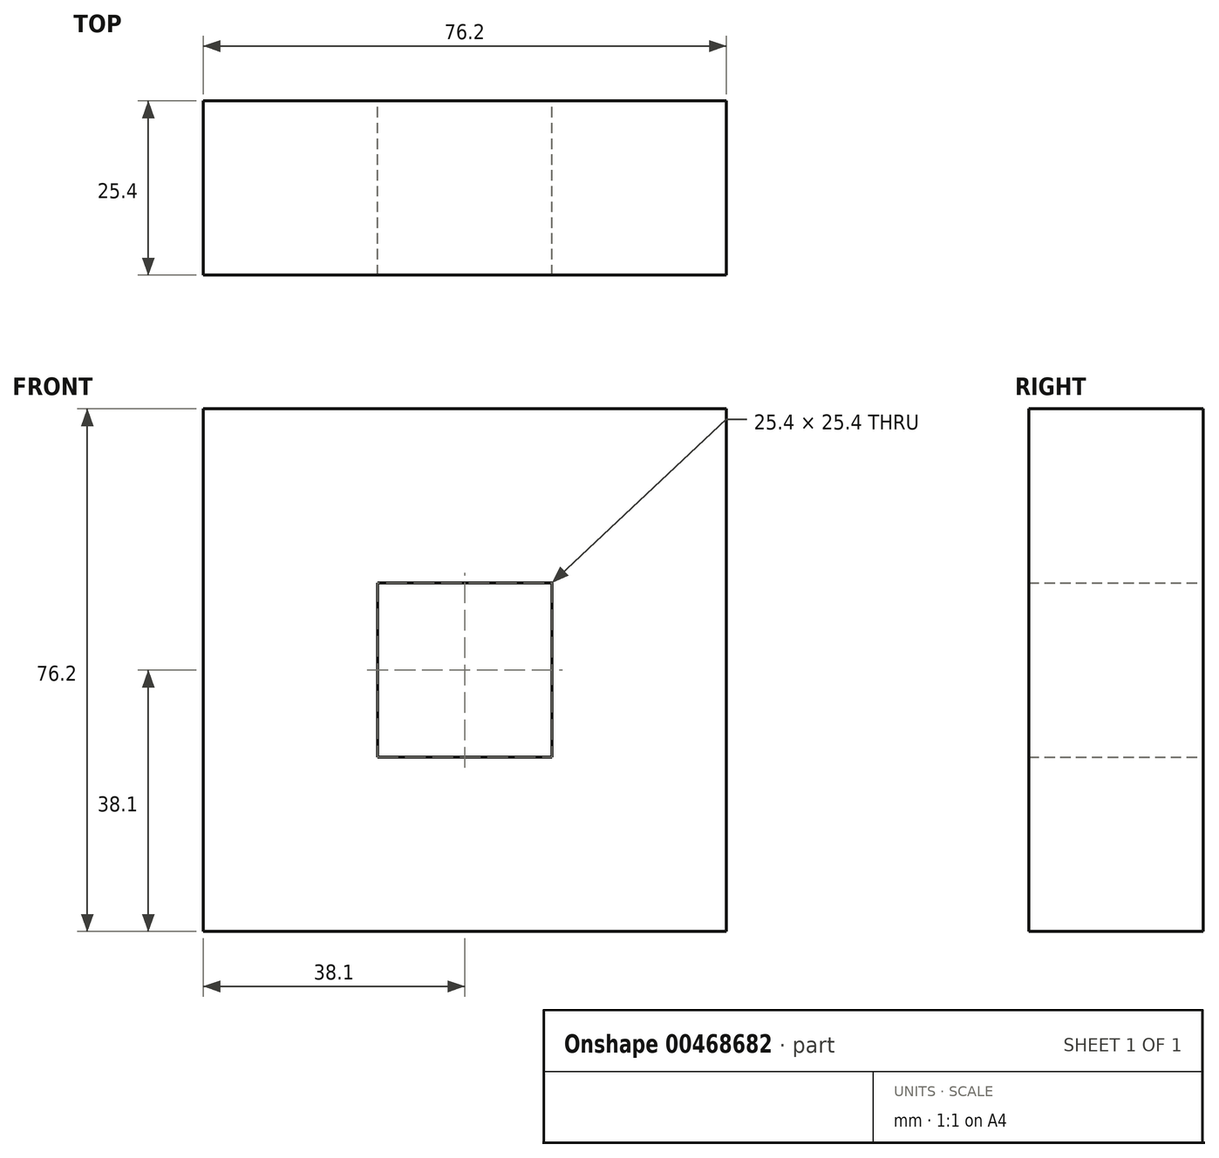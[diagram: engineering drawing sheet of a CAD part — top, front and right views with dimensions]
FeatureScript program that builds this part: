
annotation { "Feature Type Name" : "Feature", "Feature Type Description" : "" }
export const myFeature = defineFeature(function(context is Context, id is Id, definition is map)
    precondition{}
    {
        {
            var Q0;
            Q0=qCreatedBy(makeId("Front.planeOp"),FACE);
            var sketch = newSketch(context, id + "F0", { "sketchPlane" : qUnion([Q0])});
            skLineSegment(sketch, "E0.bottom", {"start": v(38.1, 38.1) * mm, "end": v(-38.1, 38.1) * mm});
            skLineSegment(sketch, "E0.top", {"start": v(38.1, -38.1) * mm, "end": v(-38.1, -38.1) * mm});
            skLineSegment(sketch, "E0.left", {"start": v(38.1, 38.1) * mm, "end": v(38.1, -38.1) * mm});
            skLineSegment(sketch, "E0.right", {"start": v(-38.1, 38.1) * mm, "end": v(-38.1, -38.1) * mm});
            skPoint(sketch, "E0.middle", {"position": v(0, 0) * mm});
            skLineSegment(sketch, "E1.bottom", {"start": v(12.7, 12.7) * mm, "end": v(-12.7, 12.7) * mm});
            skLineSegment(sketch, "E1.top", {"start": v(12.7, -12.7) * mm, "end": v(-12.7, -12.7) * mm});
            skLineSegment(sketch, "E1.left", {"start": v(12.7, 12.7) * mm, "end": v(12.7, -12.7) * mm});
            skLineSegment(sketch, "E1.right", {"start": v(-12.7, 12.7) * mm, "end": v(-12.7, -12.7) * mm});
            skLineSegment(sketch, "E2", {"start": v(-12.7, 12.7) * mm, "end": v(-12.7, 38.1) * mm});
            skLineSegment(sketch, "E3", {"start": v(-12.7, 12.7) * mm, "end": v(-38.1, 12.7) * mm});
            skLineSegment(sketch, "E4", {"start": v(-12.7, -12.7) * mm, "end": v(-38.1, -12.7) * mm});
            skLineSegment(sketch, "E5", {"start": v(12.7, -12.7) * mm, "end": v(12.7, -38.1) * mm});
            skLineSegment(sketch, "E6", {"start": v(12.7, -12.7) * mm, "end": v(38.1, -12.7) * mm});
            skLineSegment(sketch, "E7", {"start": v(12.7, 12.7) * mm, "end": v(38.1, 12.7) * mm});
            skLineSegment(sketch, "E8", {"start": v(-12.7, -12.7) * mm, "end": v(-12.7, -38.1) * mm});
            skLineSegment(sketch, "E9", {"start": v(12.7, 12.7) * mm, "end": v(12.7, 38.1) * mm});
            skSolve(sketch);
        }
        {
            var Q0;
            {var subQ3=sQuery(id+"F0.wireOp",EDGE,"E2");Q0=makeQuery(id+"F0.imprint","IMPRINT",FACE,{"disambiguationData":[TD([[makeQuery(id+"F0.imprint","IMPRINT",EDGE,{"derivedFrom":subQ3}),1.0]])]});}
            var Q1;
            Q1=makeQuery(id+"F0.imprint","IMPRINT",FACE,{"disambiguationData":[TD([[makeQuery(id+"F0.imprint","IMPRINT",EDGE,{"derivedFrom":sQuery(id+"F0.wireOp",EDGE,"E1.bottom")}),-1.0]])]});
            var Q2;
            {var subQ4=sQuery(id+"F0.wireOp",EDGE,"E7");Q2=makeQuery(id+"F0.imprint","IMPRINT",FACE,{"disambiguationData":[TD([[makeQuery(id+"F0.imprint","IMPRINT",EDGE,{"derivedFrom":subQ4}),1.0]])]});}
            var Q3;
            Q3=makeQuery(id+"F0.imprint","IMPRINT",FACE,{"disambiguationData":[TD([[makeQuery(id+"F0.imprint","IMPRINT",EDGE,{"derivedFrom":sQuery(id+"F0.wireOp",EDGE,"E1.left")}),1.0]])]});
            var Q4;
            {var subQ3=sQuery(id+"F0.wireOp",EDGE,"E5");Q4=makeQuery(id+"F0.imprint","IMPRINT",FACE,{"disambiguationData":[TD([[makeQuery(id+"F0.imprint","IMPRINT",EDGE,{"derivedFrom":subQ3}),1.0]])]});}
            var Q5;
            Q5=makeQuery(id+"F0.imprint","IMPRINT",FACE,{"disambiguationData":[TD([[makeQuery(id+"F0.imprint","IMPRINT",EDGE,{"derivedFrom":sQuery(id+"F0.wireOp",EDGE,"E1.top")}),1.0]])]});
            var Q6;
            {var subQ4=sQuery(id+"F0.wireOp",EDGE,"E4");Q6=makeQuery(id+"F0.imprint","IMPRINT",FACE,{"disambiguationData":[TD([[makeQuery(id+"F0.imprint","IMPRINT",EDGE,{"derivedFrom":subQ4}),1.0]])]});}
            var Q7;
            Q7=makeQuery(id+"F0.imprint","IMPRINT",FACE,{"disambiguationData":[TD([[makeQuery(id+"F0.imprint","IMPRINT",EDGE,{"derivedFrom":sQuery(id+"F0.wireOp",EDGE,"E1.right")}),-1.0]])]});
            extrude(context, id + "F1", {"entities" : qUnion([Q0, Q1, Q2, Q3, Q4, Q5, Q6, Q7]), "depth" : 25.4 * mm});
        }
    });
